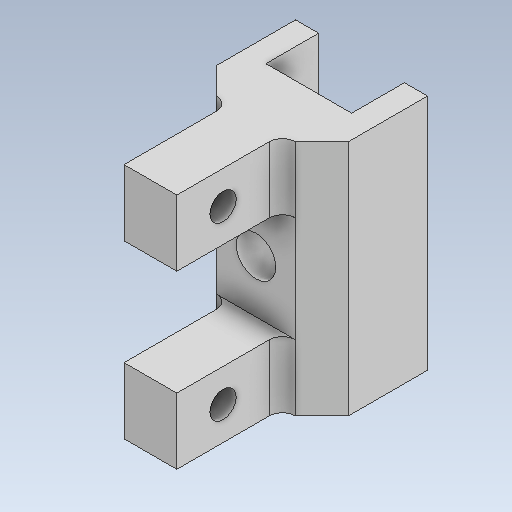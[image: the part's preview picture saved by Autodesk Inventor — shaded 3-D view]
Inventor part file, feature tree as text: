
AUTODESK INVENTOR PART (.ipt)
format: ipt  version: 2020 (Build 240168000, 168)  size: 244,736 bytes
history: native  units: mm
features: extrude x9, sketch x9, projected_geometry x9, reference x3, other x3, chamfer x1, fillet x1
ambient origin geometry x8: Origin, YZ Plane, XZ Plane, XY Plane, X Axis, Y Axis, Z Axis, Center Point
bodies: Solid1 (feature_tree)
feature tree (35):
  extrude  "Extrusion1"  Depth=10.0mm
  extrude  "Extrusion2"  Depth=3.0mm
  extrude  "Extrusion3"  Depth=1.75mm
  extrude  "Extrusion4"  Depth=1.75mm
  extrude  "Extrusion5"  Depth=4.0mm TaperAngle=0.0deg
  extrude  "Extrusion6"  Depth=5.0mm
  extrude  "Extrusion7"  Depth=5.0mm
  extrude  "Extrusion8"  Depth=8.0mm TaperAngle=0.0deg
  extrude  "Extrusion9"  Depth=3.0mm TaperAngle=0.0deg
  chamfer  "Chamfer1"  Distance=3.0mm
  fillet  "Fillet1"  Radius=3.5mm
  sketch  "Sketch1"  dims[d0=8.0mm d1=10.0mm]
  reference  "Reference1"
  sketch  "Sketch2"  dims[d2=4.0mm d3=0.0mm d4=3.0mm]
  projected_geometry  "Projected Loop1"
  sketch  "Sketch3"  dims[d5=4.0mm d6=0.0mm d7=1.75mm]
  projected_geometry  "Projected Loop2"
  reference  "Reference2"
  reference  "Reference3"
  sketch  "Sketch4"  dims[d8=8.0mm d9=1.75mm]
  projected_geometry  "Projected Loop3"
  sketch  "Sketch5"  dims[d10=8.0mm d11=4.0mm d12=0.0mm]
  projected_geometry  "Projected Loop4"
  sketch  "Sketch6"  dims[d13=10.0mm d14=5.0mm]
  projected_geometry  "Projected Loop5"
  sketch  "Sketch7"  dims[d15=10.0mm d16=5.0mm]
  projected_geometry  "Projected Loop6"
  sketch  "Sketch8"  dims[d17=8.0mm d18=0.0mm d19=8.0mm d20=0.0mm]
  projected_geometry  "Projected Loop7"
  sketch  "Sketch9"  dims[d21=8.0mm d22=0.0mm d23=3.0mm d24=0.0mm d25=3.0mm d26=0.0mm d27=3.5mm d28=2.0mm d29=3.5mm d30=2.0mm d31=4.0mm d32=0.0mm d33=2.0mm d34=2.0mm d35=45.0deg d36=1.0mm]
  projected_geometry  "Projected Loop8"
  projected_geometry  "Projected Loop9"
  parser-record x1  (decoder bookkeeping rows leaked as tree rows — omitted from the tree; the rows remain in map.json)
  other  "eye_bearing.iam"
  other  "eye_bearing_2:1"
note: 1 file-system path scrubbed to <path> (originals preserved in map.json)
